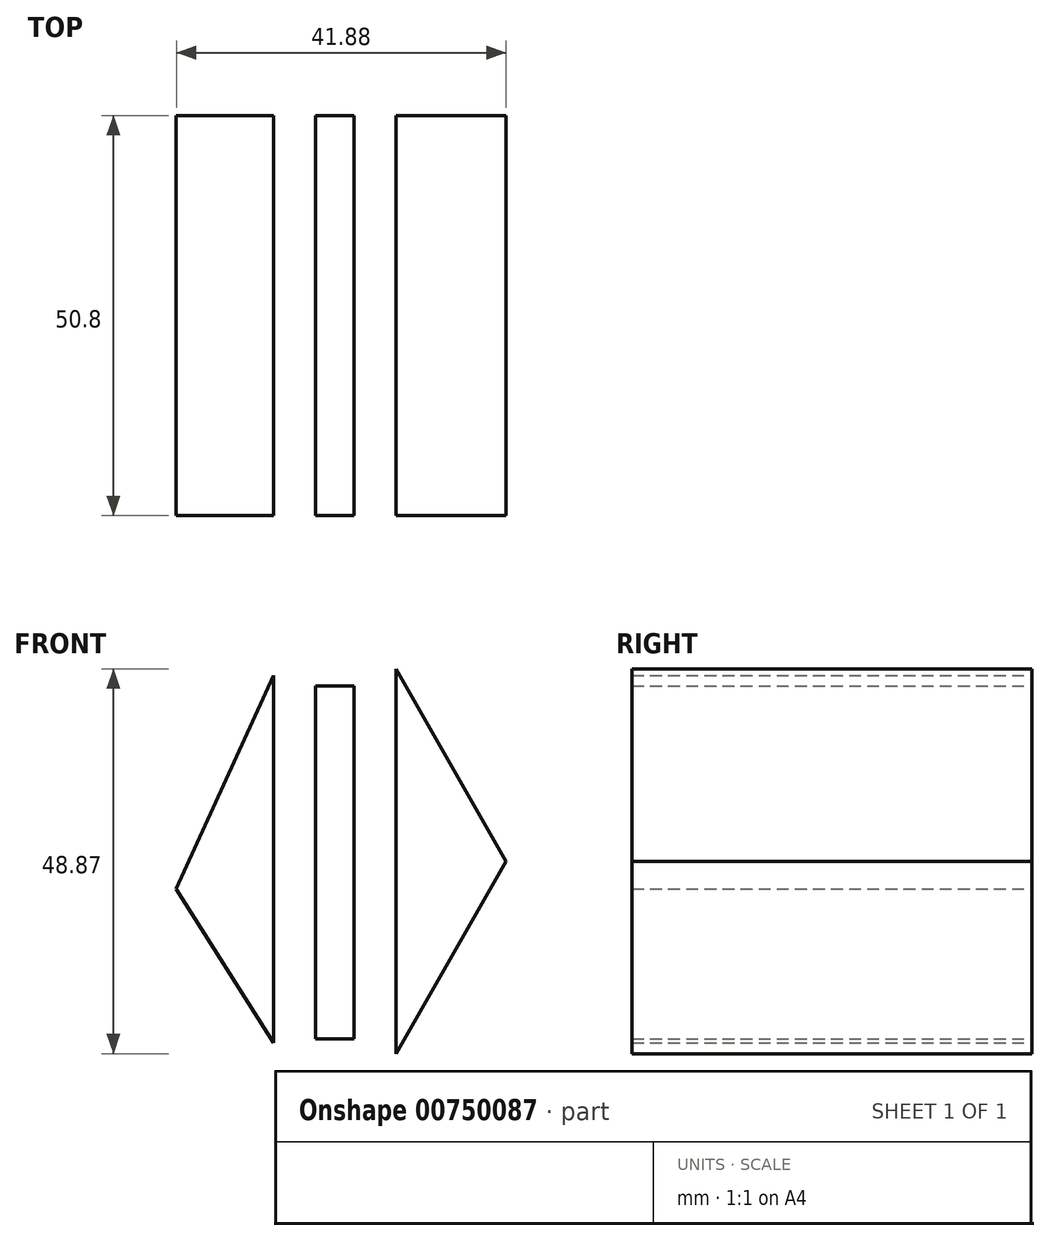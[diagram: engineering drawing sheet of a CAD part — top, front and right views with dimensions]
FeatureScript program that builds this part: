
annotation { "Feature Type Name" : "Feature", "Feature Type Description" : "" }
export const myFeature = defineFeature(function(context is Context, id is Id, definition is map)
    precondition{}
    {
        {
            var Q0;
            Q0=qCreatedBy(makeId("Front.planeOp"),FACE);
            var sketch = newSketch(context, id + "F0", { "sketchPlane" : qUnion([Q0])});
            skLineSegment(sketch, "E0", {"start": v(-23.22, 43.63) * mm, "end": v(-35.57, 16.51) * mm});
            skLineSegment(sketch, "E1", {"start": v(-35.57, 16.51) * mm, "end": v(-23.22, -3.09) * mm});
            skLineSegment(sketch, "E2", {"start": v(-23.22, 43.63) * mm, "end": v(-23.22, -3.09) * mm});
            skSolve(sketch);
        }
        {
            var Q0;
            Q0 = qSketchRegion(id + "F0", true);
            extrude(context, id + "F1", {"entities" : qUnion([Q0]), "depth" : 50.8 * mm, "offsetDistance" : 25.4 * mm});
        }
        {
            var Q0;
            Q0=qCreatedBy(makeId("Front.planeOp"),FACE);
            var sketch = newSketch(context, id + "F2", { "sketchPlane" : qUnion([Q0])});
            skLineSegment(sketch, "E3.bottom", {"start": v(-17.85, 42.29) * mm, "end": v(-13.02, 42.29) * mm});
            skLineSegment(sketch, "E3.top", {"start": v(-17.85, -2.55) * mm, "end": v(-13.02, -2.55) * mm});
            skLineSegment(sketch, "E3.left", {"start": v(-17.85, 42.29) * mm, "end": v(-17.85, -2.55) * mm});
            skLineSegment(sketch, "E3.right", {"start": v(-13.02, 42.29) * mm, "end": v(-13.02, -2.55) * mm});
            skSolve(sketch);
        }
        {
            var Q0;
            Q0 = qSketchRegion(id + "F2", true);
            extrude(context, id + "F3", {"entities" : qUnion([Q0]), "depth" : 50.8 * mm, "offsetDistance" : 25.4 * mm});
        }
        {
            var Q0;
            Q0=qCreatedBy(makeId("Front.planeOp"),FACE);
            var sketch = newSketch(context, id + "F4", { "sketchPlane" : qUnion([Q0])});
            skLineSegment(sketch, "E4", {"start": v(-7.65, 44.44) * mm, "end": v(-7.65, -4.43) * mm});
            skLineSegment(sketch, "E5", {"start": v(-7.65, -4.43) * mm, "end": v(6.3, 20) * mm});
            skPoint(sketch, "E5.endSnap0", {"position": v(-7.65, 20) * mm});
            skLineSegment(sketch, "E6", {"start": v(6.3, 20) * mm, "end": v(-7.65, 44.44) * mm});
            skSolve(sketch);
        }
        {
            var Q0;
            Q0 = qSketchRegion(id + "F4", true);
            extrude(context, id + "F5", {"entities" : qUnion([Q0]), "depth" : 50.8 * mm, "offsetDistance" : 25.4 * mm});
        }
    });
